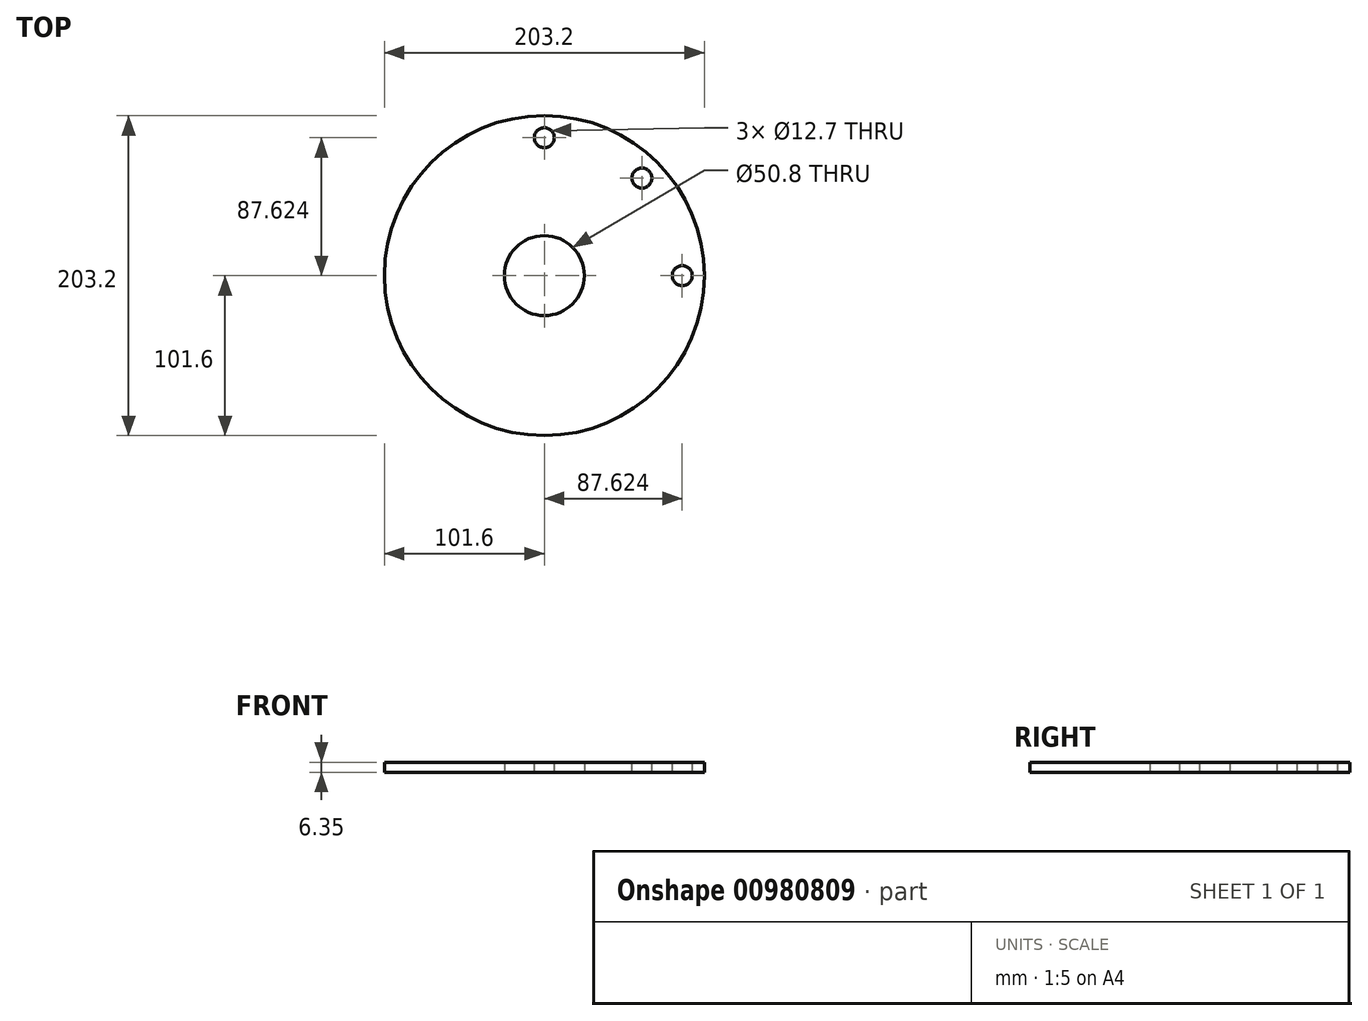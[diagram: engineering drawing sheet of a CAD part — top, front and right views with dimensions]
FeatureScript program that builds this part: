
annotation { "Feature Type Name" : "Feature", "Feature Type Description" : "" }
export const myFeature = defineFeature(function(context is Context, id is Id, definition is map)
    precondition{}
    {
        {
            var Q0;
            Q0=qCreatedBy(makeId("Top.planeOp"),FACE);
            var sketch = newSketch(context, id + "F0", { "sketchPlane" : qUnion([Q0])});
            skCircle(sketch, "E0", {"center": v(0, 0) * mm, "radius": 101.6 * mm});
            skCircle(sketch, "E1", {"center": v(0, 0) * mm, "radius": 25.4 * mm});
            skSolve(sketch);
        }
        {
            var Q0;
            Q0=makeQuery(id+"F0.imprint","IMPRINT",FACE,{"disambiguationData":[TD([[makeQuery(id+"F0.imprint","IMPRINT",EDGE,{"derivedFrom":sQuery(id+"F0.wireOp",EDGE,"E0")}),1.0]])]});
            extrude(context, id + "F1", {"entities" : qUnion([Q0]), "depth" : 6.35 * mm, "offsetDistance" : 25.4 * mm});
        }
        {
            var Q0;
            Q0=makeQuery(id+"F1.opExtrude","CAP_FACE",FACE,{"disambiguationData":[OSD([sQuery(id+"F0.wireOp",EDGE,"E0"),sQuery(id+"F0.wireOp",EDGE,"E1")])],"isStart":false});
            var sketch = newSketch(context, id + "F2", { "sketchPlane" : qUnion([Q0])});
            skCircle(sketch, "E2", {"center": v(0, 0) * mm, "radius": 87.62 * mm, "construction": true});
            skCircle(sketch, "E3", {"center": v(0, 87.62) * mm, "radius": 6.35 * mm});
            skCircle(sketch, "E4.1.0", {"center": v(61.96, 61.96) * mm, "radius": 6.35 * mm});
            skCircle(sketch, "E4.2.0", {"center": v(87.62, 0) * mm, "radius": 6.35 * mm});
            skLineSegment(sketch, "E4.anchor1", {"start": v(0, 0) * mm, "end": v(0, 87.62) * mm, "construction": true});
            skLineSegment(sketch, "E4.anchor2", {"start": v(0, 0) * mm, "end": v(87.62, 0) * mm, "construction": true});
            skSolve(sketch);
        }
        {
            var Q0;
            Q0=makeQuery(id+"F2.imprint","IMPRINT",FACE,{"disambiguationData":[TD([[makeQuery(id+"F2.imprint","IMPRINT",EDGE,{"derivedFrom":sQuery(id+"F2.wireOp",EDGE,"E3")}),1.0]])]});
            var Q1;
            Q1=makeQuery(id+"F2.imprint","IMPRINT",FACE,{"disambiguationData":[TD([[makeQuery(id+"F2.imprint","IMPRINT",EDGE,{"derivedFrom":sQuery(id+"F2.wireOp",EDGE,"E4.1.0")}),1.0]])]});
            var Q2;
            Q2=makeQuery(id+"F2.imprint","IMPRINT",FACE,{"disambiguationData":[TD([[makeQuery(id+"F2.imprint","IMPRINT",EDGE,{"derivedFrom":sQuery(id+"F2.wireOp",EDGE,"E4.2.0")}),1.0]])]});
            extrude(context, id + "F3", {"entities" : qUnion([Q0, Q1, Q2]), "operationType" : NewBodyOperationType.REMOVE, "endBound" : BoundingType.THROUGH_ALL, "oppositeDirection" : true, "depth" : 25.4 * mm, "offsetDistance" : 25.4 * mm});
        }
    });
